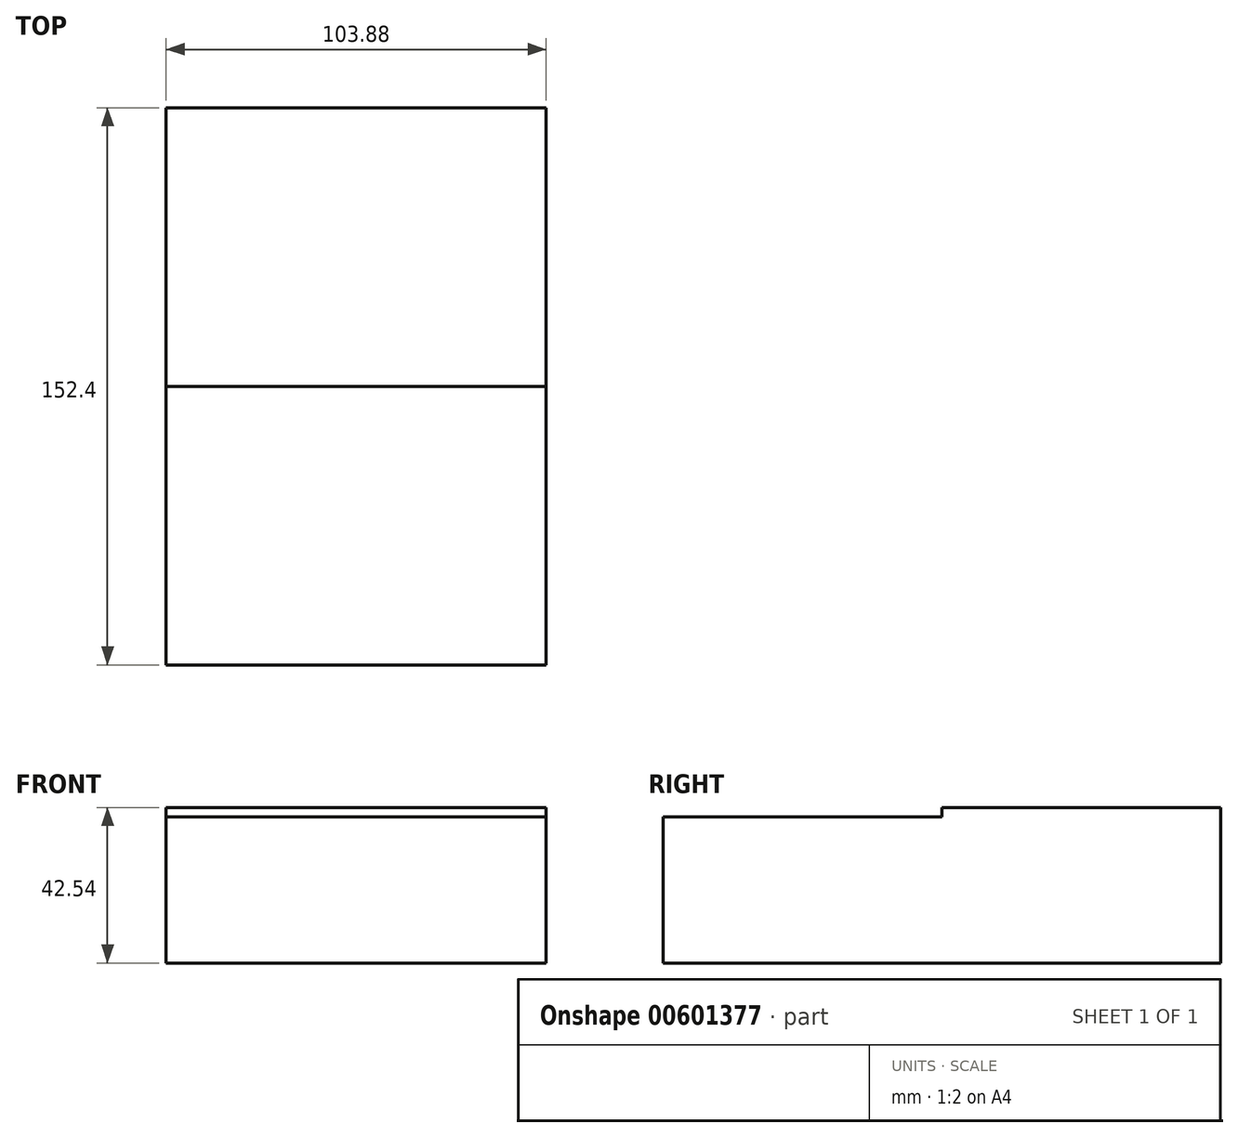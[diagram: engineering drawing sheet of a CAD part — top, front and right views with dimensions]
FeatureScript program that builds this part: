
annotation { "Feature Type Name" : "Feature", "Feature Type Description" : "" }
export const myFeature = defineFeature(function(context is Context, id is Id, definition is map)
    precondition{}
    {
        {
            var Q0;
            Q0=qCreatedBy(makeId("Front.planeOp"),FACE);
            var sketch = newSketch(context, id + "F0", { "sketchPlane" : qUnion([Q0])});
            skLineSegment(sketch, "E0.bottom", {"start": v(-51.94, 20) * mm, "end": v(51.94, 20) * mm});
            skLineSegment(sketch, "E0.top", {"start": v(-51.94, -20) * mm, "end": v(51.94, -20) * mm});
            skLineSegment(sketch, "E0.left", {"start": v(-51.94, 20) * mm, "end": v(-51.94, -20) * mm});
            skLineSegment(sketch, "E0.right", {"start": v(51.94, 20) * mm, "end": v(51.94, -20) * mm});
            skPoint(sketch, "E0.middle", {"position": v(0, 0) * mm});
            skSolve(sketch);
        }
        {
            var Q0;
            Q0=makeQuery(id+"F0.imprint","IMPRINT",FACE,{"disambiguationData":[TD([[makeQuery(id+"F0.imprint","IMPRINT",EDGE,{"derivedFrom":sQuery(id+"F0.wireOp",EDGE,"E0.bottom")}),-1.0]])]});
            extrude(context, id + "F1", {"entities" : qUnion([Q0]), "depth" : 152.4 * mm, "offsetDistance" : 25.4 * mm});
        }
        {
            var Q0;
            Q0=makeQuery(id+"F1.opExtrude","SWEPT_FACE",FACE,{"disambiguationData":[OSD([sQuery(id+"F0.wireOp",EDGE,"E0.bottom")])]});
            var sketch = newSketch(context, id + "F2", { "sketchPlane" : qUnion([Q0])});
            skLineSegment(sketch, "E1", {"start": v(-51.94, -76.2) * mm, "end": v(51.94, -76.2) * mm});
            skSolve(sketch);
        }
        {
            var Q0;
            {var subQ0=sQuery(id+"F2.wireOp",EDGE,"E1");Q0=makeQuery(id+"F2.imprint","IMPRINT",FACE,{"disambiguationData":[TD([[makeQuery(id+"F2.imprint","IMPRINT",EDGE,{"derivedFrom":subQ0}),1.0]])]});}
            extrude(context, id + "F3", {"entities" : qUnion([Q0]), "operationType" : NewBodyOperationType.ADD, "depth" : 2.54 * mm, "offsetDistance" : 25.4 * mm});
        }
    });
